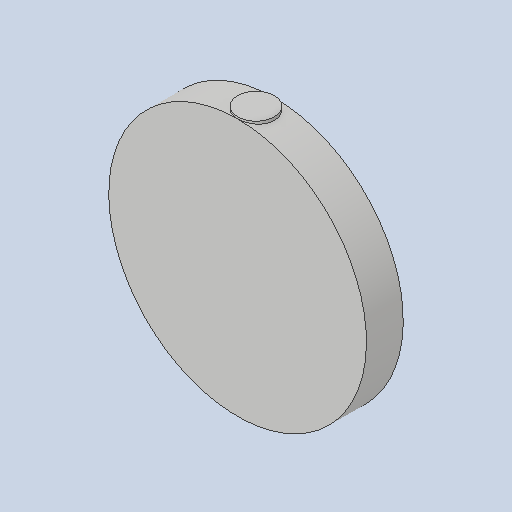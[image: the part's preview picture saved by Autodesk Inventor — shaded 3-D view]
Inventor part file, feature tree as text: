
AUTODESK INVENTOR PART (.ipt)
format: ipt  version: 2024.2 (Build 282272000, 272)  size: 96,256 bytes
history: native  units: mm
features: extrude x2, sketch x2, other x1
ambient origin geometry x8: Origin, YZ Plane, XZ Plane, XY Plane, X Axis, Y Axis, Z Axis, Center Point
bodies: Body1 (feature_tree)
feature tree (5):
  other  "Твердое тело1"
  extrude  "Выдавливание1"  Depth=140.0mm
  extrude  "Выдавливание2"  Depth=20.0mm TaperAngle=0.0deg
  sketch  "Эскиз3"
  sketch  "Эскиз4"
